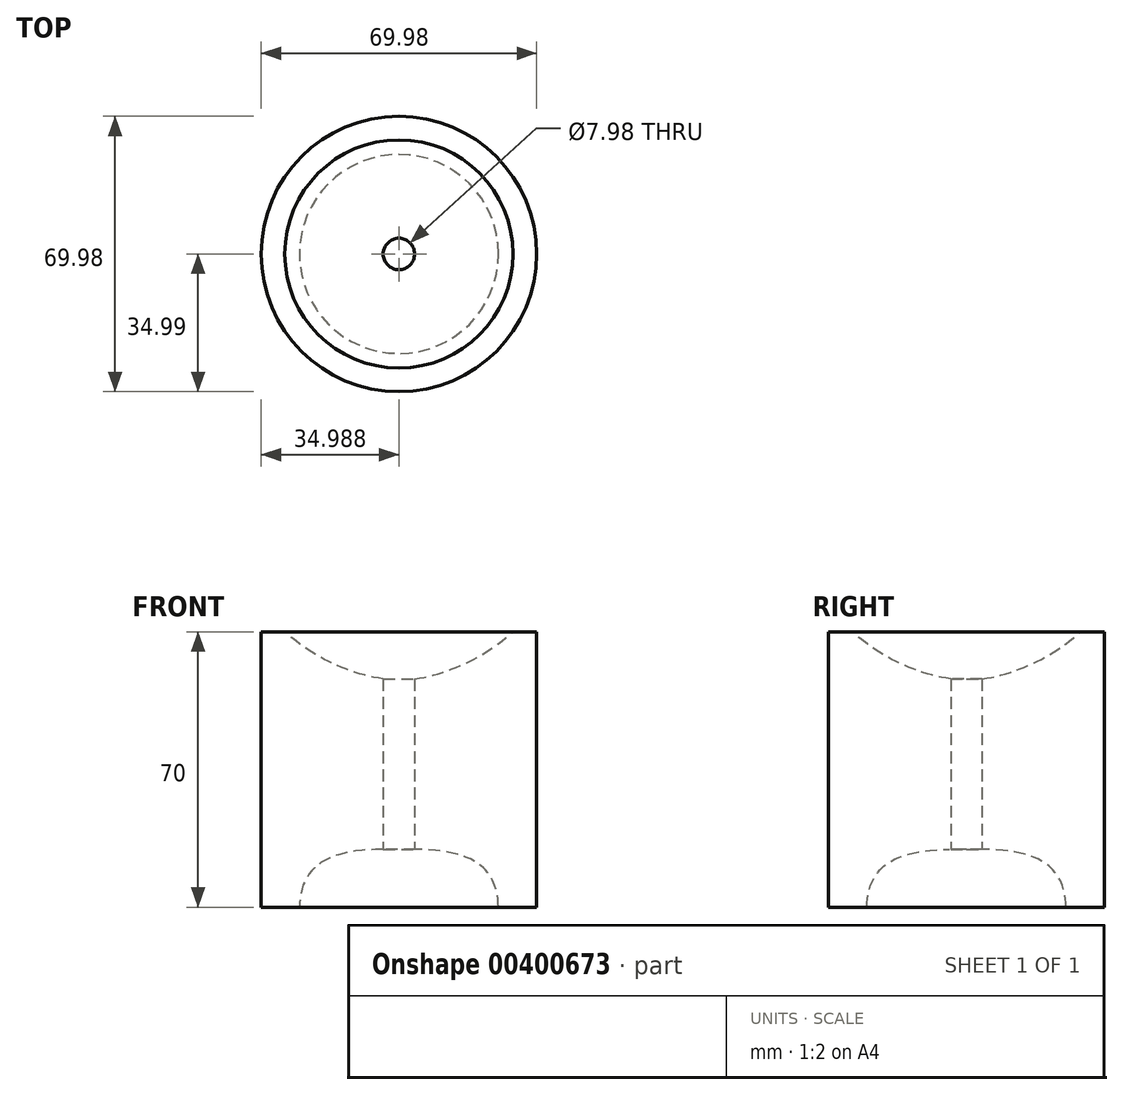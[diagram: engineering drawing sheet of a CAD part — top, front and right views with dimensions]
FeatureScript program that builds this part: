
annotation { "Feature Type Name" : "Feature", "Feature Type Description" : "" }
export const myFeature = defineFeature(function(context is Context, id is Id, definition is map)
    precondition{}
    {
        {
            var Q0;
            Q0=qCreatedBy(makeId("Front.planeOp"),FACE);
            var sketch = newSketch(context, id + "F0", { "sketchPlane" : qUnion([Q0])});
            skLineSegment(sketch, "E0.bottom", {"start": v(0, 0) * mm, "end": v(9.7, 0) * mm});
            skLineSegment(sketch, "E0.top", {"start": v(0, 70) * mm, "end": v(6, 70) * mm});
            skLineSegment(sketch, "E0.left", {"start": v(0, 0) * mm, "end": v(0, 70) * mm});
            skLineSegment(sketch, "E0.right", {"start": v(31, 14.7) * mm, "end": v(31, 58) * mm});
            skLineSegment(sketch, "E1", {"start": v(34.99, 14.7) * mm, "end": v(34.99, 58) * mm});
            skArc(sketch, "E2", {"start": v(6, 70) * mm, "mid": v(17.63, 62.18) * mm, "end": v(31, 58) * mm});
            skFitSpline(sketch, "E3", {"points": [v(31, 14.7) * mm, v(9.7, 0) * mm], "startDerivative": vector(-45.08, 0.2) * mm, "endDerivative": vector(-0.63, -29.3) * mm});
            skLineSegment(sketch, "E4", {"start": v(31, 14.7) * mm, "end": v(34.99, 14.7) * mm});
            skLineSegment(sketch, "E5", {"start": v(31, 58) * mm, "end": v(34.99, 58) * mm});
            skSolve(sketch);
        }
        {
            var Q0;
            Q0=makeQuery(id+"F0.imprint","IMPRINT",FACE,{"disambiguationData":[TD([[makeQuery(id+"F0.imprint","IMPRINT",EDGE,{"derivedFrom":sQuery(id+"F0.wireOp",EDGE,"E0.left")}),-1.0]])]});
            var Q1;
            Q1=sQuery(id+"F0.wireOp",EDGE,"E1");
            revolve(context, id + "F1", {"entities" : qUnion([Q0]), "axis" : qUnion([Q1]), "revolveType" : RevolveType.FULL});
        }
    });
